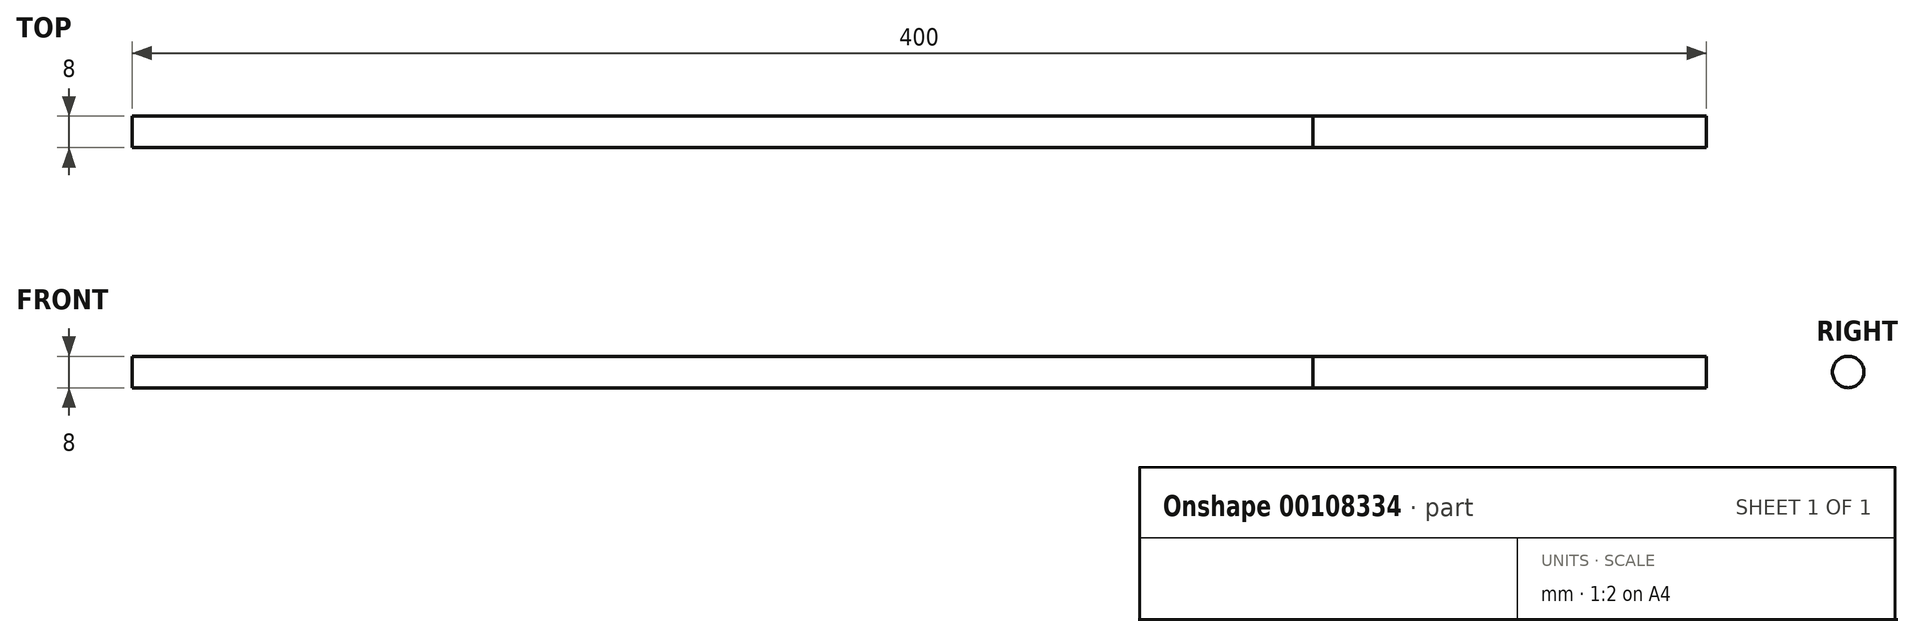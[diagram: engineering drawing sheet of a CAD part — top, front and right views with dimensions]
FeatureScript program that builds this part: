
annotation { "Feature Type Name" : "Feature", "Feature Type Description" : "" }
export const myFeature = defineFeature(function(context is Context, id is Id, definition is map)
    precondition{}
    {
        {
            var Q0;
            Q0=qCreatedBy(makeId("Right.planeOp"),FACE);
            var sketch = newSketch(context, id + "F0", { "sketchPlane" : qUnion([Q0])});
            skCircle(sketch, "E0", {"center": v(0, 0) * mm, "radius": 4 * mm});
            skSolve(sketch);
        }
        {
            var Q0;
            Q0=makeQuery(id+"F0.imprint","IMPRINT",FACE,{"disambiguationData":[TD([[makeQuery(id+"F0.imprint","IMPRINT",EDGE,{"derivedFrom":sQuery(id+"F0.wireOp",EDGE,"E0")}),1.0]])]});
            extrude(context, id + "F1", {"entities" : qUnion([Q0]), "depth" : 300 * mm});
        }
        {
            var Q0;
            Q0 = qSketchRegion(id + "F0", true);
            extrude(context, id + "F2", {"entities" : qUnion([Q0]), "depth" : 400 * mm});
        }
        {
            var Q0;
            Q0 = qSketchRegion(id + "F0", true);
            extrude(context, id + "F3", {"entities" : qUnion([Q0]), "depth" : 300 * mm});
        }
    });
